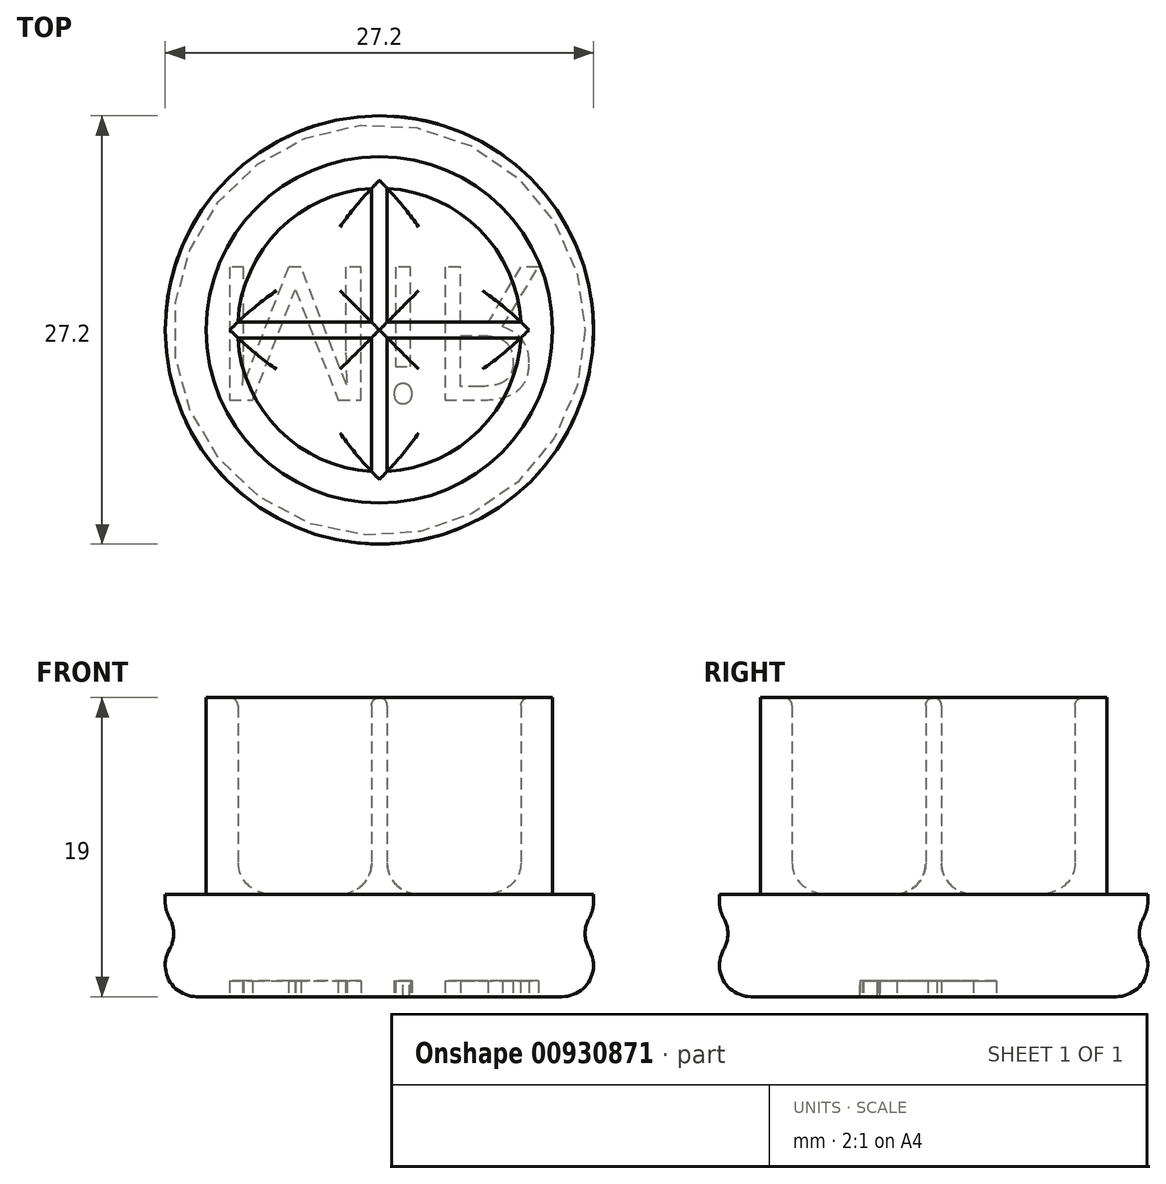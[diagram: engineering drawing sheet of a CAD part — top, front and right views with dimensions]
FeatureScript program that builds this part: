
annotation { "Feature Type Name" : "Feature", "Feature Type Description" : "" }
export const myFeature = defineFeature(function(context is Context, id is Id, definition is map)
    precondition{}
    {
        {
            var Q0;
            Q0=qCreatedBy(makeId("Top.planeOp"),FACE);
            var sketch = newSketch(context, id + "F0", { "sketchPlane" : qUnion([Q0])});
            skCircle(sketch, "E0", {"center": v(0, 0) * mm, "radius": 11 * mm});
            skCircle(sketch, "E1", {"center": v(0, 0) * mm, "radius": 9 * mm});
            skCircle(sketch, "E2", {"center": v(0, 0) * mm, "radius": 13.6 * mm});
            skSolve(sketch);
        }
        {
            var Q0;
            Q0 = qSketchRegion(id + "F0", true);
            var Q1;
            Q1=makeQuery(id+"F0.imprint","IMPRINT",FACE,{"disambiguationData":[TD([[makeQuery(id+"F0.imprint","IMPRINT",EDGE,{"derivedFrom":sQuery(id+"F0.wireOp",EDGE,"E0")}),1.0]])]});
            var Q2;
            Q2=makeQuery(id+"F0.imprint","IMPRINT",FACE,{"disambiguationData":[TD([[makeQuery(id+"F0.imprint","IMPRINT",EDGE,{"derivedFrom":sQuery(id+"F0.wireOp",EDGE,"E1")}),1.0]])]});
            extrude(context, id + "F1", {"entities" : qUnion([Q0, Q1, Q2]), "depth" : 2.5 * mm, "offsetDistance" : 25 * mm});
        }
        {
            var Q0;
            Q0=makeQuery(id+"F0.imprint","IMPRINT",FACE,{"disambiguationData":[TD([[makeQuery(id+"F0.imprint","IMPRINT",EDGE,{"derivedFrom":sQuery(id+"F0.wireOp",EDGE,"E0")}),1.0]])]});
            extrude(context, id + "F2", {"entities" : qUnion([Q0]), "operationType" : NewBodyOperationType.ADD, "depth" : 15 * mm, "offsetDistance" : 25 * mm});
        }
        {
            var Q0;
            Q0=makeQuery(id+"F2.boolean.opBoolean","SPLIT",FACE,{"disambiguationData":[TD([makeQuery(id+"F2.opExtrude","SWEPT_FACE",FACE,{"disambiguationData":[OSD([sQuery(id+"F0.wireOp",EDGE,"E1")])]})])],"derivedFrom":makeQuery(id+"F1.opExtrude","CAP_FACE",FACE,{"disambiguationData":[OSD([sQuery(id+"F0.wireOp",EDGE,"E2")])],"isStart":false})});
            var sketch = newSketch(context, id + "F3", { "sketchPlane" : qUnion([Q0])});
            skLineSegment(sketch, "E3", {"start": v(-0.5, 8.99) * mm, "end": v(-0.5, 0.5) * mm});
            skLineSegment(sketch, "E4", {"start": v(-8.99, 0.5) * mm, "end": v(-0.5, 0.5) * mm});
            skLineSegment(sketch, "E5", {"start": v(0.5, 8.99) * mm, "end": v(0.5, 0.5) * mm});
            skLineSegment(sketch, "E6", {"start": v(-8.99, -0.5) * mm, "end": v(-0.5, -0.5) * mm});
            skLineSegment(sketch, "E7.trimOffspring", {"start": v(0.5, 0.5) * mm, "end": v(8.99, 0.5) * mm});
            skLineSegment(sketch, "E8.trimOffspring", {"start": v(0.5, -0.5) * mm, "end": v(8.99, -0.5) * mm});
            skLineSegment(sketch, "E9.trimOffspring", {"start": v(-0.5, -0.5) * mm, "end": v(-0.5, -8.99) * mm});
            skLineSegment(sketch, "E10.trimOffspring", {"start": v(0.5, -0.5) * mm, "end": v(0.5, -8.99) * mm});
            skSolve(sketch);
        }
        {
            var Q0;
            {var subQ3=sQuery(id+"F3.wireOp",EDGE,"E3");Q0=makeQuery(id+"F3.imprint","IMPRINT",FACE,{"disambiguationData":[TD([[makeQuery(id+"F3.imprint","IMPRINT",EDGE,{"derivedFrom":subQ3}),1.0]])]});}
            extrude(context, id + "F4", {"entities" : qUnion([Q0]), "operationType" : NewBodyOperationType.ADD, "depth" : 12.5 * mm, "offsetDistance" : 25 * mm});
        }
        {
            var Q0;
            Q0=makeQuery(id+"F4.opExtrude","CAP_EDGE",EDGE,{"disambiguationData":[OSD([sQuery(id+"F3.wireOp",EDGE,"E4")])],"isStart":true});
            var Q1;
            {var subQ0=makeQuery(id+"F1.opExtrude","CAP_FACE",FACE,{"disambiguationData":[OSD([sQuery(id+"F0.wireOp",EDGE,"E2")])],"isStart":false});var subQ1=makeQuery(id+"F2.opExtrude","SWEPT_FACE",FACE,{"disambiguationData":[OSD([sQuery(id+"F0.wireOp",EDGE,"E1")])]});Q1=makeQuery(id+"F4.boolean.opBoolean","SPLIT",EDGE,{"disambiguationData":[TD([makeQuery(id+"F4.opExtrude","SWEPT_FACE",FACE,{"disambiguationData":[OSD([sQuery(id+"F3.wireOp",EDGE,"E3")])]})])],"derivedFrom":makeQuery(id+"F2.boolean.opBoolean","INTERSECT",EDGE,{"derivedFrom":[subQ0,subQ1]})});}
            var Q2;
            Q2=makeQuery(id+"F4.opExtrude","CAP_EDGE",EDGE,{"disambiguationData":[OSD([sQuery(id+"F3.wireOp",EDGE,"E3")])],"isStart":true});
            var Q3;
            {var subQ0=makeQuery(id+"F2.opExtrude","SWEPT_FACE",FACE,{"disambiguationData":[OSD([sQuery(id+"F0.wireOp",EDGE,"E1")])]});Q3=makeQuery(id+"F4.boolean.opBoolean","SPLIT",FACE,{"disambiguationData":[TD([makeQuery(id+"F4.opExtrude","SWEPT_FACE",FACE,{"disambiguationData":[OSD([sQuery(id+"F3.wireOp",EDGE,"E5")])]})])],"derivedFrom":makeQuery(id+"F2.boolean.opBoolean","SPLIT",FACE,{"disambiguationData":[TD([subQ0])],"derivedFrom":makeQuery(id+"F1.opExtrude","CAP_FACE",FACE,{"disambiguationData":[OSD([sQuery(id+"F0.wireOp",EDGE,"E2")])],"isStart":false})})});}
            var Q4;
            {var subQ0=makeQuery(id+"F2.opExtrude","SWEPT_FACE",FACE,{"disambiguationData":[OSD([sQuery(id+"F0.wireOp",EDGE,"E1")])]});Q4=makeQuery(id+"F4.boolean.opBoolean","SPLIT",FACE,{"disambiguationData":[TD([makeQuery(id+"F4.opExtrude","SWEPT_FACE",FACE,{"disambiguationData":[OSD([sQuery(id+"F3.wireOp",EDGE,"E8.trimOffspring")])]})])],"derivedFrom":makeQuery(id+"F2.boolean.opBoolean","SPLIT",FACE,{"disambiguationData":[TD([subQ0])],"derivedFrom":makeQuery(id+"F1.opExtrude","CAP_FACE",FACE,{"disambiguationData":[OSD([sQuery(id+"F0.wireOp",EDGE,"E2")])],"isStart":false})})});}
            var Q5;
            {var subQ0=makeQuery(id+"F2.opExtrude","SWEPT_FACE",FACE,{"disambiguationData":[OSD([sQuery(id+"F0.wireOp",EDGE,"E1")])]});Q5=makeQuery(id+"F4.boolean.opBoolean","SPLIT",FACE,{"disambiguationData":[TD([makeQuery(id+"F4.opExtrude","SWEPT_FACE",FACE,{"disambiguationData":[OSD([sQuery(id+"F3.wireOp",EDGE,"E6")])]})])],"derivedFrom":makeQuery(id+"F2.boolean.opBoolean","SPLIT",FACE,{"disambiguationData":[TD([subQ0])],"derivedFrom":makeQuery(id+"F1.opExtrude","CAP_FACE",FACE,{"disambiguationData":[OSD([sQuery(id+"F0.wireOp",EDGE,"E2")])],"isStart":false})})});}
            fillet(context, id + "F5", {"entities" : qUnion([Q0, Q1, Q2, Q3, Q4, Q5]), "radius" : 2 * mm, "tangentPropagation" : true, "allowEdgeOverflow" : false});
        }
        {
            var Q0;
            Q0=makeQuery(id+"F4.opExtrude","CAP_EDGE",EDGE,{"disambiguationData":[OSD([sQuery(id+"F3.wireOp",EDGE,"E4")])],"isStart":false});
            var Q1;
            {var subQ1=sQuery(id+"F3.wireOp",EDGE,"E3");var subQ2=sQuery(id+"F0.wireOp",EDGE,"E1");Q1=makeQuery(id+"F4.boolean.opBoolean","SPLIT",EDGE,{"disambiguationData":[TD([makeQuery(id+"F4.opExtrude","SWEPT_FACE",FACE,{"disambiguationData":[OSD([subQ1])]})])],"derivedFrom":makeQuery(id+"F2.opExtrude","CAP_EDGE",EDGE,{"disambiguationData":[OSD([subQ2])],"isStart":false})});}
            var Q2;
            Q2=makeQuery(id+"F4.opExtrude","CAP_EDGE",EDGE,{"disambiguationData":[OSD([sQuery(id+"F3.wireOp",EDGE,"E3")])],"isStart":false});
            var Q3;
            {var subQ0=sQuery(id+"F3.wireOp",EDGE,"E5");var subQ1=makeQuery(id+"F4.opExtrude","SWEPT_FACE",FACE,{"disambiguationData":[OSD([subQ0])]});var subQ2=sQuery(id+"F0.wireOp",EDGE,"E2");var subQ3=makeQuery(id+"F1.opExtrude","CAP_FACE",FACE,{"disambiguationData":[OSD([subQ2])],"isStart":false});var subQ4=sQuery(id+"F0.wireOp",EDGE,"E1");var subQ7=makeQuery(id+"F2.opExtrude","SWEPT_FACE",FACE,{"disambiguationData":[OSD([subQ4])]});Q3=makeQuery(id+"F5.opFillet","BLEND_EDGE",EDGE,{"blendedFrom":[makeQuery(id+"F4.boolean.opBoolean","SPLIT",EDGE,{"disambiguationData":[TD([subQ1])],"derivedFrom":makeQuery(id+"F2.boolean.opBoolean","INTERSECT",EDGE,{"derivedFrom":[subQ3,subQ7]})}),makeQuery(id+"F4.boolean.opBoolean","SPLIT",FACE,{"disambiguationData":[TD([subQ1])],"derivedFrom":subQ7})],"blendedInto":[makeQuery(id+"F4.boolean.opBoolean","SPLIT",FACE,{"disambiguationData":[TD([subQ1])],"derivedFrom":subQ7})]});}
            var Q4;
            Q4=makeQuery(id+"F4.opExtrude","CAP_EDGE",EDGE,{"disambiguationData":[OSD([sQuery(id+"F3.wireOp",EDGE,"E5")])],"isStart":false});
            var Q5;
            Q5=makeQuery(id+"F4.opExtrude","CAP_EDGE",EDGE,{"disambiguationData":[OSD([sQuery(id+"F3.wireOp",EDGE,"E7.trimOffspring")])],"isStart":false});
            var Q6;
            {var subQ0=sQuery(id+"F3.wireOp",EDGE,"E8.trimOffspring");var subQ2=sQuery(id+"F0.wireOp",EDGE,"E1");Q6=makeQuery(id+"F4.boolean.opBoolean","SPLIT",EDGE,{"disambiguationData":[TD([makeQuery(id+"F4.opExtrude","SWEPT_FACE",FACE,{"disambiguationData":[OSD([subQ0])]})])],"derivedFrom":makeQuery(id+"F2.opExtrude","CAP_EDGE",EDGE,{"disambiguationData":[OSD([subQ2])],"isStart":false})});}
            var Q7;
            {var subQ0=sQuery(id+"F3.wireOp",EDGE,"E8.trimOffspring");Q7=makeQuery(id+"F5.opFillet","BLEND_EDGE",EDGE,{"blendedFrom":[makeQuery(id+"F4.opExtrude","CAP_EDGE",EDGE,{"disambiguationData":[OSD([subQ0])],"isStart":true}),makeQuery(id+"F4.opExtrude","SWEPT_FACE",FACE,{"disambiguationData":[OSD([subQ0])]})],"blendedInto":[makeQuery(id+"F4.opExtrude","SWEPT_FACE",FACE,{"disambiguationData":[OSD([subQ0])]})]});}
            var Q8;
            Q8=makeQuery(id+"F4.opExtrude","CAP_EDGE",EDGE,{"disambiguationData":[OSD([sQuery(id+"F3.wireOp",EDGE,"E10.trimOffspring")])],"isStart":false});
            var Q9;
            Q9=makeQuery(id+"F4.opExtrude","CAP_EDGE",EDGE,{"disambiguationData":[OSD([sQuery(id+"F3.wireOp",EDGE,"E9.trimOffspring")])],"isStart":false});
            var Q10;
            Q10=makeQuery(id+"F4.opExtrude","CAP_EDGE",EDGE,{"disambiguationData":[OSD([sQuery(id+"F3.wireOp",EDGE,"E6")])],"isStart":false});
            var Q11;
            {var subQ0=sQuery(id+"F3.wireOp",EDGE,"E6");var subQ2=sQuery(id+"F0.wireOp",EDGE,"E1");Q11=makeQuery(id+"F4.boolean.opBoolean","SPLIT",EDGE,{"disambiguationData":[TD([makeQuery(id+"F4.opExtrude","SWEPT_FACE",FACE,{"disambiguationData":[OSD([subQ0])]})])],"derivedFrom":makeQuery(id+"F2.opExtrude","CAP_EDGE",EDGE,{"disambiguationData":[OSD([subQ2])],"isStart":false})});}
            var Q12;
            {var subQ1=sQuery(id+"F3.wireOp",EDGE,"E5");var subQ2=sQuery(id+"F0.wireOp",EDGE,"E1");Q12=makeQuery(id+"F4.boolean.opBoolean","SPLIT",EDGE,{"disambiguationData":[TD([makeQuery(id+"F4.opExtrude","SWEPT_FACE",FACE,{"disambiguationData":[OSD([subQ1])]})])],"derivedFrom":makeQuery(id+"F2.opExtrude","CAP_EDGE",EDGE,{"disambiguationData":[OSD([subQ2])],"isStart":false})});}
            var Q13;
            Q13=makeQuery(id+"F4.opExtrude","CAP_EDGE",EDGE,{"disambiguationData":[OSD([sQuery(id+"F3.wireOp",EDGE,"E8.trimOffspring")])],"isStart":false});
            fillet(context, id + "F6", {"entities" : qUnion([Q0, Q1, Q2, Q3, Q4, Q5, Q6, Q7, Q8, Q9, Q10, Q11, Q12, Q13]), "radius" : 0.5 * mm, "tangentPropagation" : true, "allowEdgeOverflow" : false});
        }
        {
            var Q0;
            Q0=makeQuery(id+"F1.opExtrude","CAP_EDGE",EDGE,{"disambiguationData":[OSD([sQuery(id+"F0.wireOp",EDGE,"E2")])],"isStart":true});
            fillet(context, id + "F7", {"entities" : qUnion([Q0]), "radius" : 2 * mm, "tangentPropagation" : true, "allowEdgeOverflow" : false});
        }
        {
            var Q0;
            Q0=makeQuery(id+"F0.imprint","IMPRINT",FACE,{"disambiguationData":[TD([[makeQuery(id+"F0.imprint","IMPRINT",EDGE,{"derivedFrom":sQuery(id+"F0.wireOp",EDGE,"E1")}),1.0]])]});
            var Q1;
            Q1=makeQuery(id+"F0.imprint","IMPRINT",FACE,{"disambiguationData":[TD([[makeQuery(id+"F0.imprint","IMPRINT",EDGE,{"derivedFrom":sQuery(id+"F0.wireOp",EDGE,"E0")}),1.0]])]});
            var Q2;
            Q2=makeQuery(id+"F0.imprint","IMPRINT",FACE,{"disambiguationData":[TD([[makeQuery(id+"F0.imprint","IMPRINT",EDGE,{"derivedFrom":sQuery(id+"F0.wireOp",EDGE,"E0")}),-1.0]])]});
            extrude(context, id + "F8", {"entities" : qUnion([Q0, Q1, Q2]), "operationType" : NewBodyOperationType.ADD, "oppositeDirection" : true, "depth" : 4 * mm, "offsetDistance" : 25 * mm});
        }
        {
            var Q0;
            Q0=makeQuery(id+"F8.opExtrude","CAP_EDGE",EDGE,{"disambiguationData":[OSD([sQuery(id+"F0.wireOp",EDGE,"E2")])],"isStart":true});
            var Q1;
            Q1=makeQuery(id+"F8.opExtrude","CAP_EDGE",EDGE,{"disambiguationData":[OSD([sQuery(id+"F0.wireOp",EDGE,"E2")])],"isStart":false});
            fillet(context, id + "F9", {"entities" : qUnion([Q0, Q1]), "radius" : 2 * mm, "tangentPropagation" : true, "allowEdgeOverflow" : false});
        }
        {
            var Q0;
            Q0=makeQuery(id+"F9.opFillet","BLEND_FACE",FACE,{"disambiguationData":[OSD([sQuery(id+"F0.wireOp",EDGE,"E2")])]});
            fillet(context, id + "F10", {"entities" : qUnion([Q0]), "radius" : 2 * mm, "tangentPropagation" : true, "allowEdgeOverflow" : false});
        }
        {
            var Q0;
            Q0=makeQuery(id+"F8.opExtrude","CAP_FACE",FACE,{"disambiguationData":[OSD([sQuery(id+"F0.wireOp",EDGE,"E2")])],"isStart":false});
            var sketch = newSketch(context, id + "F11", { "sketchPlane" : qUnion([Q0])});
            skText(sketch, "E11", { "text": "MiR", "fontName": "OpenSans-Regular.ttf"});
            const initialGuessF11  = {"E11": [-0.01068, -0.004, 1, 0, 0.00852]};
            skSetInitialGuess(sketch, initialGuessF11);
            skSolve(sketch);
        }
        {
            var Q0;
            Q0 = qSketchRegion(id + "F11", true);
            extrude(context, id + "F12", {"entities" : qUnion([Q0]), "operationType" : NewBodyOperationType.REMOVE, "oppositeDirection" : true, "depth" : 1 * mm, "offsetDistance" : 25 * mm});
        }
    });
